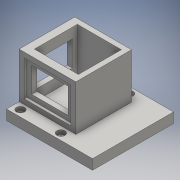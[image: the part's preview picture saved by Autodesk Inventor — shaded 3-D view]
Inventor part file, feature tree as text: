
AUTODESK INVENTOR PART (.ipt)
format: ipt  version: 2016 (Build 200138000, 138)  size: 186,368 bytes
history: native  units: mm
features: sketch x7, extrude x6, hole x1
ambient origin geometry x8: Origin, YZ Plane, XZ Plane, XY Plane, X Axis, Y Axis, Z Axis, Center Point
bodies: Solid1 (feature_tree)
feature tree (14):
  extrude  "Extrusion1"  Depth=42.5mm
  hole  "Hole1"  [1 undecoded]
  extrude  "Extrusion2"  Depth=40.0mm
  extrude  "Extrusion3"  Depth=67.5mm
  extrude  "Extrusion4"  Depth=56.0mm
  extrude  "Extrusion5"  Depth=2.5mm
  extrude  "Extrusion6"  Depth=5.0mm
  sketch  "Sketch1"  dims[d0=85.0mm d1=42.5mm]
  sketch  "Sketch2"  dims[d2=80.0mm d3=40.0mm]
  sketch  "Sketch3"  dims[d4=10.0mm d5=0.0mm d6=40.0mm]
  sketch  "Sketch4"  dims[d7=67.5mm d8=33.75mm]
  sketch  "Sketch5"  dims[d9=7.5mm]
  sketch  "Sketch6"  dims[d10=4.5mm d11=6.0mm d12=8.0mm d13=4.0mm d14=14.3117mm d15=8.0mm d16=20.594885mm d17=56.0mm]
  sketch  "Sketch7"  dims[d18=55.0mm d19=27.5mm d20=5.0mm d21=5.0mm d22=7.5mm d23=7.5mm d24=45.0mm d25=0.0mm d27=5.0mm d28=5.0mm d29=5.0mm d30=5.0mm d31=2.5mm d32=0.0mm d33=5.0mm d34=5.0mm d35=5.0mm d36=5.0mm d37=45.0mm d38=0.0mm d39=5.0mm d40=5.0mm d41=5.0mm d42=5.0mm d43=2.5mm d44=0.0mm d45=5.0mm d46=5.0mm d47=5.0mm d48=5.0mm d49=2.5mm d50=0.0mm]
note: 1 required parameter value undecoded (feature->parameter linkage not recoverable at this tier; creation-order binding heuristic only, values carry confidence <= 0.55)
